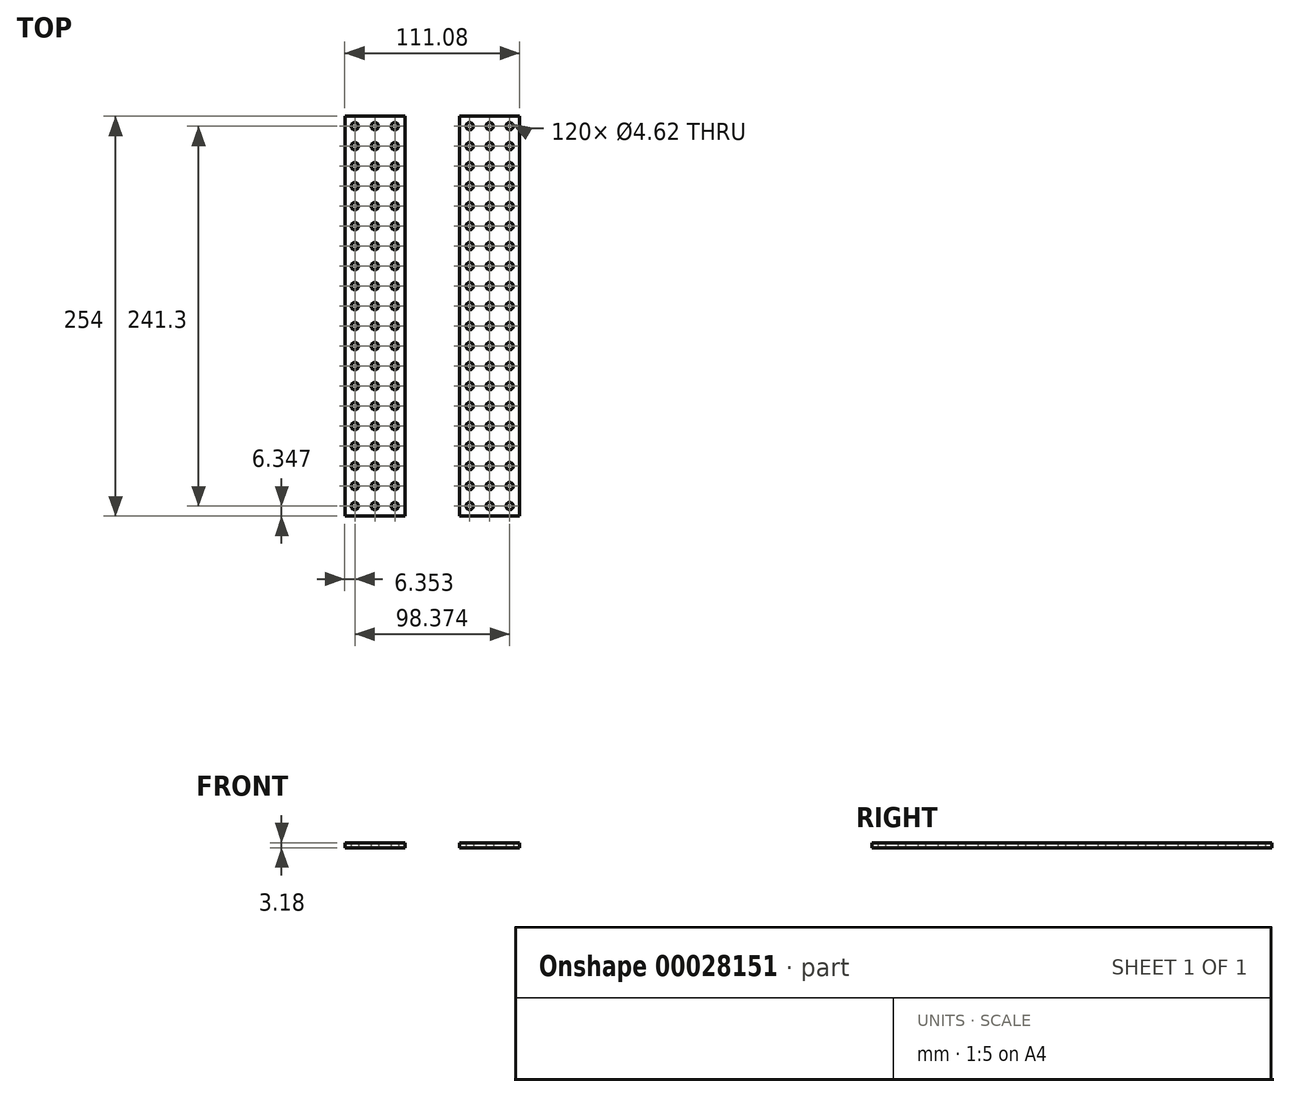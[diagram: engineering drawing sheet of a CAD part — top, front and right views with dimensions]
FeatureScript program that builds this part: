
annotation { "Feature Type Name" : "Feature", "Feature Type Description" : "" }
export const myFeature = defineFeature(function(context is Context, id is Id, definition is map)
    precondition{}
    {
        {
            var Q0;
            Q0=qCreatedBy(makeId("Top.planeOp"),FACE);
            var sketch = newSketch(context, id + "F0", { "sketchPlane" : qUnion([Q0])});
            skLineSegment(sketch, "E0", {"start": v(-55.54, 154.36) * mm, "end": v(-55.54, -99.64) * mm});
            skLineSegment(sketch, "E1", {"start": v(-55.54, -99.64) * mm, "end": v(-17.44, -99.64) * mm});
            skCircle(sketch, "E2", {"center": v(-49.19, 97.2) * mm, "radius": 2.31 * mm});
            skCircle(sketch, "E3", {"center": v(-49.19, -93.3) * mm, "radius": 2.31 * mm});
            skCircle(sketch, "E4", {"center": v(-49.19, 84.5) * mm, "radius": 2.31 * mm});
            skCircle(sketch, "E5", {"center": v(-49.19, 71.8) * mm, "radius": 2.31 * mm});
            skCircle(sketch, "E6", {"center": v(-49.19, 59.1) * mm, "radius": 2.31 * mm});
            skCircle(sketch, "E7", {"center": v(-49.19, 46.4) * mm, "radius": 2.31 * mm});
            skCircle(sketch, "E8", {"center": v(-49.19, 33.7) * mm, "radius": 2.31 * mm});
            skCircle(sketch, "E9", {"center": v(-49.19, 21) * mm, "radius": 2.31 * mm});
            skCircle(sketch, "E10", {"center": v(-49.19, 8.3) * mm, "radius": 2.31 * mm});
            skCircle(sketch, "E11", {"center": v(-49.19, -4.4) * mm, "radius": 2.31 * mm});
            skCircle(sketch, "E12", {"center": v(-49.19, -17.1) * mm, "radius": 2.31 * mm});
            skCircle(sketch, "E13", {"center": v(-49.19, -29.8) * mm, "radius": 2.31 * mm});
            skCircle(sketch, "E14", {"center": v(-49.19, -42.5) * mm, "radius": 2.31 * mm});
            skCircle(sketch, "E15", {"center": v(-49.19, -55.2) * mm, "radius": 2.31 * mm});
            skCircle(sketch, "E16", {"center": v(-49.19, -67.9) * mm, "radius": 2.31 * mm});
            skCircle(sketch, "E17", {"center": v(-49.19, -80.6) * mm, "radius": 2.31 * mm});
            skLineSegment(sketch, "E18", {"start": v(-55.54, 154.36) * mm, "end": v(-17.44, 154.36) * mm});
            skCircle(sketch, "E19.MirrorC", {"center": v(-36.49, 33.7) * mm, "radius": 2.31 * mm});
            skCircle(sketch, "E20.MirrorC", {"center": v(-36.49, -67.9) * mm, "radius": 2.31 * mm});
            skCircle(sketch, "E21.MirrorC", {"center": v(-36.49, -80.6) * mm, "radius": 2.31 * mm});
            skCircle(sketch, "E22.MirrorC", {"center": v(-36.49, -29.8) * mm, "radius": 2.31 * mm});
            skCircle(sketch, "E23.MirrorC", {"center": v(-36.49, 84.5) * mm, "radius": 2.31 * mm});
            skCircle(sketch, "E24.MirrorC", {"center": v(-36.49, 46.4) * mm, "radius": 2.31 * mm});
            skCircle(sketch, "E25.MirrorC", {"center": v(-36.49, -55.2) * mm, "radius": 2.31 * mm});
            skCircle(sketch, "E26.MirrorC", {"center": v(-36.49, -42.5) * mm, "radius": 2.31 * mm});
            skCircle(sketch, "E27.MirrorC", {"center": v(-36.49, 8.3) * mm, "radius": 2.31 * mm});
            skCircle(sketch, "E28.MirrorC", {"center": v(-36.49, 59.1) * mm, "radius": 2.31 * mm});
            skCircle(sketch, "E29.MirrorC", {"center": v(-36.49, -4.4) * mm, "radius": 2.31 * mm});
            skCircle(sketch, "E30.MirrorC", {"center": v(-36.49, 21) * mm, "radius": 2.31 * mm});
            skCircle(sketch, "E31.MirrorC", {"center": v(-36.49, 71.8) * mm, "radius": 2.31 * mm});
            skCircle(sketch, "E32.MirrorC", {"center": v(-36.49, 97.2) * mm, "radius": 2.31 * mm});
            skCircle(sketch, "E33.MirrorC", {"center": v(-36.49, -17.1) * mm, "radius": 2.31 * mm});
            skCircle(sketch, "E34.MirrorC", {"center": v(-36.49, -93.3) * mm, "radius": 2.31 * mm});
            skCircle(sketch, "E35.MirrorC", {"center": v(-23.79, -17.1) * mm, "radius": 2.31 * mm});
            skCircle(sketch, "E36.MirrorC", {"center": v(-23.79, 8.3) * mm, "radius": 2.31 * mm});
            skCircle(sketch, "E37.MirrorC", {"center": v(-23.79, -93.3) * mm, "radius": 2.31 * mm});
            skCircle(sketch, "E38.MirrorC", {"center": v(-23.79, -67.9) * mm, "radius": 2.31 * mm});
            skCircle(sketch, "E39.MirrorC", {"center": v(-23.79, -4.4) * mm, "radius": 2.31 * mm});
            skCircle(sketch, "E40.MirrorC", {"center": v(-23.79, 97.2) * mm, "radius": 2.31 * mm});
            skCircle(sketch, "E41.MirrorC", {"center": v(-23.79, -42.5) * mm, "radius": 2.31 * mm});
            skCircle(sketch, "E42.MirrorC", {"center": v(-23.79, 33.7) * mm, "radius": 2.31 * mm});
            skCircle(sketch, "E43.MirrorC", {"center": v(-23.79, 59.1) * mm, "radius": 2.31 * mm});
            skCircle(sketch, "E44.MirrorC", {"center": v(-23.79, -55.2) * mm, "radius": 2.31 * mm});
            skCircle(sketch, "E45.MirrorC", {"center": v(-23.79, 84.5) * mm, "radius": 2.31 * mm});
            skCircle(sketch, "E46.MirrorC", {"center": v(-23.79, 46.4) * mm, "radius": 2.31 * mm});
            skCircle(sketch, "E47.MirrorC", {"center": v(-23.79, -29.8) * mm, "radius": 2.31 * mm});
            skCircle(sketch, "E48.MirrorC", {"center": v(-23.79, -80.6) * mm, "radius": 2.31 * mm});
            skCircle(sketch, "E49.MirrorC", {"center": v(-23.79, 71.8) * mm, "radius": 2.31 * mm});
            skCircle(sketch, "E50.MirrorC", {"center": v(-23.79, 21) * mm, "radius": 2.31 * mm});
            skLineSegment(sketch, "E51", {"start": v(-17.44, 154.36) * mm, "end": v(-17.44, -99.64) * mm});
            skLineSegment(sketch, "E52", {"start": v(-55.54, 154.36) * mm, "end": v(-49.19, 154.36) * mm});
            skCircle(sketch, "E53", {"center": v(-49.19, 148) * mm, "radius": 2.31 * mm});
            skCircle(sketch, "E54", {"center": v(-36.49, 148) * mm, "radius": 2.31 * mm});
            skCircle(sketch, "E55", {"center": v(-23.79, 148) * mm, "radius": 2.31 * mm});
            skCircle(sketch, "E56", {"center": v(-49.19, 135.3) * mm, "radius": 2.31 * mm});
            skCircle(sketch, "E57", {"center": v(-49.19, 122.6) * mm, "radius": 2.31 * mm});
            skCircle(sketch, "E58", {"center": v(-49.19, 109.9) * mm, "radius": 2.31 * mm});
            skCircle(sketch, "E59", {"center": v(-36.49, 135.3) * mm, "radius": 2.31 * mm});
            skCircle(sketch, "E60", {"center": v(-23.79, 135.3) * mm, "radius": 2.31 * mm});
            skCircle(sketch, "E61", {"center": v(-36.49, 122.6) * mm, "radius": 2.31 * mm});
            skCircle(sketch, "E62", {"center": v(-23.79, 122.6) * mm, "radius": 2.31 * mm});
            skCircle(sketch, "E63", {"center": v(-36.49, 109.9) * mm, "radius": 2.31 * mm});
            skCircle(sketch, "E64", {"center": v(-23.79, 109.9) * mm, "radius": 2.31 * mm});
            skSolve(sketch);
        }
        {
            var Q0;
            Q0=makeQuery(id+"F0.imprint","IMPRINT",FACE,{"disambiguationData":[TD([[makeQuery(id+"F0.imprint","IMPRINT",EDGE,{"derivedFrom":sQuery(id+"F0.wireOp",EDGE,"E0")}),1.0]])]});
            extrude(context, id + "F1", {"entities" : qUnion([Q0]), "depth" : 3.17 * mm});
        }
        {
            var Q0;
            Q0=makeQuery(id+"F1.opExtrude","SWEPT_BODY",BODY,{"disambiguationData":[OSD([sQuery(id+"F0.wireOp",EDGE,"E0"),sQuery(id+"F0.wireOp",EDGE,"E1"),sQuery(id+"F0.wireOp",EDGE,"E2"),sQuery(id+"F0.wireOp",EDGE,"E3"),sQuery(id+"F0.wireOp",EDGE,"E4"),sQuery(id+"F0.wireOp",EDGE,"E5"),sQuery(id+"F0.wireOp",EDGE,"E6"),sQuery(id+"F0.wireOp",EDGE,"E7"),sQuery(id+"F0.wireOp",EDGE,"E8"),sQuery(id+"F0.wireOp",EDGE,"E9"),sQuery(id+"F0.wireOp",EDGE,"E10"),sQuery(id+"F0.wireOp",EDGE,"E11"),sQuery(id+"F0.wireOp",EDGE,"E12"),sQuery(id+"F0.wireOp",EDGE,"E13"),sQuery(id+"F0.wireOp",EDGE,"E14"),sQuery(id+"F0.wireOp",EDGE,"E15"),sQuery(id+"F0.wireOp",EDGE,"E16"),sQuery(id+"F0.wireOp",EDGE,"E17"),sQuery(id+"F0.wireOp",EDGE,"E18"),sQuery(id+"F0.wireOp",EDGE,"E19.MirrorC"),sQuery(id+"F0.wireOp",EDGE,"E20.MirrorC"),sQuery(id+"F0.wireOp",EDGE,"E21.MirrorC"),sQuery(id+"F0.wireOp",EDGE,"E22.MirrorC"),sQuery(id+"F0.wireOp",EDGE,"E23.MirrorC"),sQuery(id+"F0.wireOp",EDGE,"E24.MirrorC"),sQuery(id+"F0.wireOp",EDGE,"E25.MirrorC"),sQuery(id+"F0.wireOp",EDGE,"E26.MirrorC"),sQuery(id+"F0.wireOp",EDGE,"E27.MirrorC"),sQuery(id+"F0.wireOp",EDGE,"E28.MirrorC"),sQuery(id+"F0.wireOp",EDGE,"E29.MirrorC"),sQuery(id+"F0.wireOp",EDGE,"E30.MirrorC"),sQuery(id+"F0.wireOp",EDGE,"E31.MirrorC"),sQuery(id+"F0.wireOp",EDGE,"E32.MirrorC"),sQuery(id+"F0.wireOp",EDGE,"E33.MirrorC"),sQuery(id+"F0.wireOp",EDGE,"E34.MirrorC"),sQuery(id+"F0.wireOp",EDGE,"E35.MirrorC"),sQuery(id+"F0.wireOp",EDGE,"E36.MirrorC"),sQuery(id+"F0.wireOp",EDGE,"E37.MirrorC"),sQuery(id+"F0.wireOp",EDGE,"E38.MirrorC"),sQuery(id+"F0.wireOp",EDGE,"E39.MirrorC"),sQuery(id+"F0.wireOp",EDGE,"E40.MirrorC"),sQuery(id+"F0.wireOp",EDGE,"E41.MirrorC"),sQuery(id+"F0.wireOp",EDGE,"E42.MirrorC"),sQuery(id+"F0.wireOp",EDGE,"E43.MirrorC"),sQuery(id+"F0.wireOp",EDGE,"E44.MirrorC"),sQuery(id+"F0.wireOp",EDGE,"E45.MirrorC"),sQuery(id+"F0.wireOp",EDGE,"E46.MirrorC"),sQuery(id+"F0.wireOp",EDGE,"E47.MirrorC"),sQuery(id+"F0.wireOp",EDGE,"E48.MirrorC"),sQuery(id+"F0.wireOp",EDGE,"E49.MirrorC"),sQuery(id+"F0.wireOp",EDGE,"E50.MirrorC"),sQuery(id+"F0.wireOp",EDGE,"E51")])]});
            var Q1;
            Q1=qCreatedBy(makeId("Right.planeOp"),FACE);
            mirror(context, id + "F2", {"entities" : qUnion([Q0]), "mirrorPlane" : qUnion([Q1])});
        }
    });
